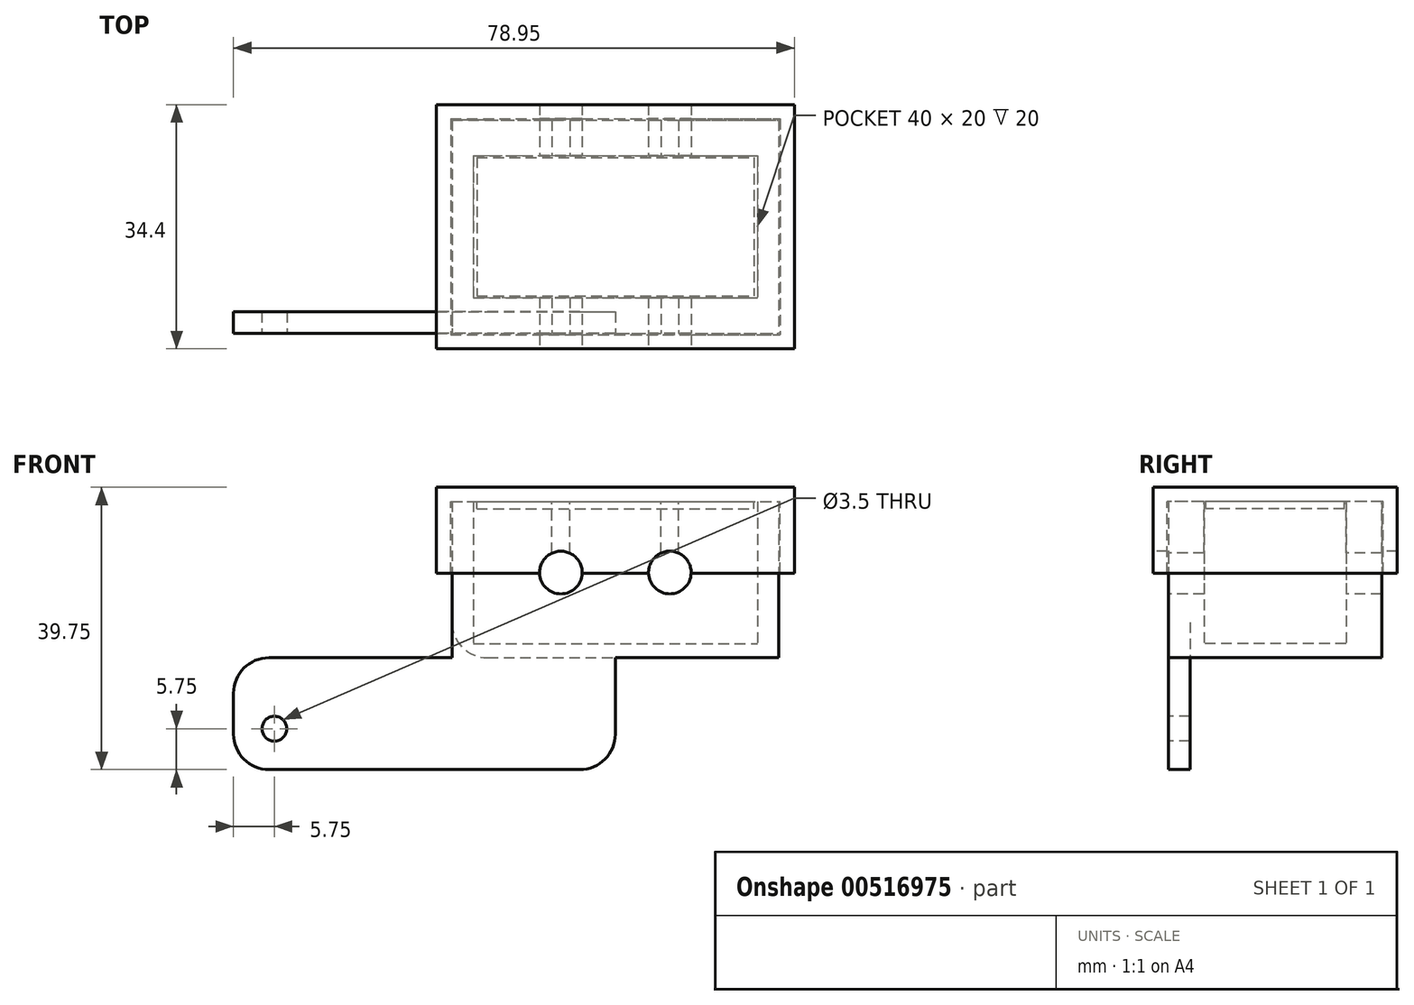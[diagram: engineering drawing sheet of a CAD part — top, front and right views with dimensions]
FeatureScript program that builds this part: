
annotation { "Feature Type Name" : "Feature", "Feature Type Description" : "" }
export const myFeature = defineFeature(function(context is Context, id is Id, definition is map)
    precondition{}
    {
        {
            var Q0;
            Q0=qCreatedBy(makeId("Top.planeOp"),FACE);
            var sketch = newSketch(context, id + "F0", { "sketchPlane" : qUnion([Q0])});
            skLineSegment(sketch, "E0.bottom", {"start": v(-20, 10) * mm, "end": v(20, 10) * mm});
            skLineSegment(sketch, "E0.top", {"start": v(-20, -10) * mm, "end": v(20, -10) * mm});
            skLineSegment(sketch, "E0.left", {"start": v(-20, 10) * mm, "end": v(-20, -10) * mm});
            skLineSegment(sketch, "E0.right", {"start": v(20, 10) * mm, "end": v(20, -10) * mm});
            skPoint(sketch, "E0.middle", {"position": v(0, 0) * mm});
            skLineSegment(sketch, "E1.bottom", {"start": v(-23, 15) * mm, "end": v(23, 15) * mm});
            skLineSegment(sketch, "E1.top", {"start": v(-23, -15) * mm, "end": v(23, -15) * mm});
            skLineSegment(sketch, "E1.left", {"start": v(-23, 15) * mm, "end": v(-23, -15) * mm});
            skLineSegment(sketch, "E1.right", {"start": v(23, 15) * mm, "end": v(23, -15) * mm});
            skSolve(sketch);
        }
        {
            var Q0;
            Q0=makeQuery(id+"F0.imprint","IMPRINT",FACE,{"disambiguationData":[TD([[makeQuery(id+"F0.imprint","IMPRINT",EDGE,{"derivedFrom":sQuery(id+"F0.wireOp",EDGE,"E0.bottom")}),1.0]])]});
            extrude(context, id + "F1", {"entities" : qUnion([Q0]), "depth" : 20 * mm, "offsetDistance" : 25 * mm});
        }
        {
            var Q0;
            Q0=makeQuery(id+"F1.opExtrude","SWEPT_FACE",FACE,{"disambiguationData":[OSD([sQuery(id+"F0.wireOp",EDGE,"E1.top")])]});
            var sketch = newSketch(context, id + "F2", { "sketchPlane" : qUnion([Q0])});
            skLineSegment(sketch, "E2", {"start": v(-23, 10) * mm, "end": v(-7.67, 10) * mm, "construction": true});
            skLineSegment(sketch, "E3", {"start": v(-7.67, 10) * mm, "end": v(7.67, 10) * mm, "construction": true});
            skLineSegment(sketch, "E4", {"start": v(7.67, 10) * mm, "end": v(23, 10) * mm, "construction": true});
            skCircle(sketch, "E5", {"center": v(-7.67, 10) * mm, "radius": 2.1 * mm});
            skCircle(sketch, "E6", {"center": v(7.67, 10) * mm, "radius": 2.1 * mm});
            skSolve(sketch);
        }
        {
            var Q0;
            Q0=makeQuery(id+"F2.imprint","IMPRINT",FACE,{"disambiguationData":[TD([[makeQuery(id+"F2.imprint","IMPRINT",EDGE,{"derivedFrom":sQuery(id+"F2.wireOp",EDGE,"E5")}),1.0]])]});
            var Q1;
            Q1=makeQuery(id+"F2.imprint","IMPRINT",FACE,{"disambiguationData":[TD([[makeQuery(id+"F2.imprint","IMPRINT",EDGE,{"derivedFrom":sQuery(id+"F2.wireOp",EDGE,"E6")}),1.0]])]});
            extrude(context, id + "F3", {"entities" : qUnion([Q0, Q1]), "operationType" : NewBodyOperationType.REMOVE, "endBound" : BoundingType.THROUGH_ALL, "oppositeDirection" : true, "depth" : 25 * mm, "offsetDistance" : 25 * mm});
        }
        {
            var Q0;
            Q0=makeQuery(id+"F1.opExtrude","SWEPT_FACE",FACE,{"disambiguationData":[OSD([sQuery(id+"F0.wireOp",EDGE,"E1.top")])]});
            var sketch = newSketch(context, id + "F4", { "sketchPlane" : qUnion([Q0])});
            skLineSegment(sketch, "E7.0.0", {"start": v(23, 0) * mm, "end": v(-23, 0) * mm, "construction": true});
            skLineSegment(sketch, "E7.0.1", {"start": v(-23, 0) * mm, "end": v(-23, 20) * mm, "construction": true});
            skLineSegment(sketch, "E7.0.2", {"start": v(-23, 20) * mm, "end": v(23, 20) * mm, "construction": true});
            skLineSegment(sketch, "E7.0.3", {"start": v(23, 20) * mm, "end": v(23, 0) * mm, "construction": true});
            skCircle(sketch, "E8.0", {"center": v(-7.67, 10) * mm, "radius": 2.1 * mm, "construction": true});
            skCircle(sketch, "E8.1", {"center": v(7.67, 10) * mm, "radius": 2.1 * mm, "construction": true});
            skLineSegment(sketch, "E9.bottom", {"start": v(-8.92, 10) * mm, "end": v(-6.42, 10) * mm});
            skLineSegment(sketch, "E9.top", {"start": v(-8.92, 23.75) * mm, "end": v(-6.42, 23.75) * mm});
            skLineSegment(sketch, "E9.left", {"start": v(-8.92, 23.75) * mm, "end": v(-8.92, 10) * mm});
            skLineSegment(sketch, "E9.right", {"start": v(-6.42, 23.75) * mm, "end": v(-6.42, 10) * mm});
            skLineSegment(sketch, "E10.bottom", {"start": v(6.42, 10) * mm, "end": v(8.92, 10) * mm});
            skLineSegment(sketch, "E10.top", {"start": v(6.42, 23.75) * mm, "end": v(8.92, 23.75) * mm});
            skLineSegment(sketch, "E10.left", {"start": v(6.42, 23.75) * mm, "end": v(6.42, 10) * mm});
            skLineSegment(sketch, "E10.right", {"start": v(8.92, 23.75) * mm, "end": v(8.92, 10) * mm});
            skSolve(sketch);
        }
        {
            var Q0;
            Q0 = qSketchRegion(id + "F4", true);
            extrude(context, id + "F5", {"entities" : qUnion([Q0]), "operationType" : NewBodyOperationType.REMOVE, "endBound" : BoundingType.THROUGH_ALL, "oppositeDirection" : true, "depth" : 25 * mm, "offsetDistance" : 25 * mm});
        }
        {
            var Q0;
            Q0=makeQuery(id+"F1.opExtrude","CAP_FACE",FACE,{"disambiguationData":[OSD([sQuery(id+"F0.wireOp",EDGE,"E0.bottom"),sQuery(id+"F0.wireOp",EDGE,"E0.top"),sQuery(id+"F0.wireOp",EDGE,"E0.left"),sQuery(id+"F0.wireOp",EDGE,"E0.right"),sQuery(id+"F0.wireOp",EDGE,"E1.bottom"),sQuery(id+"F0.wireOp",EDGE,"E1.top"),sQuery(id+"F0.wireOp",EDGE,"E1.left"),sQuery(id+"F0.wireOp",EDGE,"E1.right")])],"isStart":true});
            var sketch = newSketch(context, id + "F6", { "sketchPlane" : qUnion([Q0])});
            skLineSegment(sketch, "E11.0.0", {"start": v(-23, -15) * mm, "end": v(23, -15) * mm});
            skLineSegment(sketch, "E11.0.1", {"start": v(23, -15) * mm, "end": v(23, 15) * mm});
            skLineSegment(sketch, "E11.0.2", {"start": v(23, 15) * mm, "end": v(-23, 15) * mm});
            skLineSegment(sketch, "E11.0.3", {"start": v(-23, 15) * mm, "end": v(-23, -15) * mm});
            skSolve(sketch);
        }
        {
            var Q0;
            Q0 = qSketchRegion(id + "F6", true);
            extrude(context, id + "F7", {"entities" : qUnion([Q0]), "operationType" : NewBodyOperationType.ADD, "depth" : 2 * mm, "offsetDistance" : 25 * mm});
        }
        {
            var Q0;
            Q0=makeQuery(id+"F7.boolean.opBoolean","MERGE",FACE,{"derivedFrom":[makeQuery(id+"F1.opExtrude","SWEPT_FACE",FACE,{"disambiguationData":[OSD([sQuery(id+"F0.wireOp",EDGE,"E1.top")])]}),makeQuery(id+"F7.opExtrude","SWEPT_FACE",FACE,{"disambiguationData":[OSD([sQuery(id+"F6.wireOp",EDGE,"E11.0.2")])]})]});
            var sketch = newSketch(context, id + "F8", { "sketchPlane" : qUnion([Q0])});
            skLineSegment(sketch, "E12.bottom", {"start": v(0, -2) * mm, "end": v(-53.75, -2) * mm});
            skLineSegment(sketch, "E12.top", {"start": v(0, -17.75) * mm, "end": v(-53.75, -17.75) * mm});
            skLineSegment(sketch, "E12.left", {"start": v(0, -2) * mm, "end": v(0, -17.75) * mm});
            skLineSegment(sketch, "E12.right", {"start": v(-53.75, -2) * mm, "end": v(-53.75, -17.75) * mm});
            skLineSegment(sketch, "E13", {"start": v(-60.63, -12) * mm, "end": v(52.21, -12) * mm, "construction": true});
            skCircle(sketch, "E14", {"center": v(-48, -12) * mm, "radius": 1.75 * mm});
            skSolve(sketch);
        }
        {
            var Q0;
            Q0 = qSketchRegion(id + "F8", true);
            extrude(context, id + "F9", {"entities" : qUnion([Q0]), "operationType" : NewBodyOperationType.ADD, "oppositeDirection" : true, "depth" : 3 * mm, "offsetDistance" : 25 * mm});
        }
        {
            var Q0;
            Q0=makeQuery(id+"F9.opExtrude","SWEPT_EDGE",EDGE,{"disambiguationData":[OSD([sQuery(id+"F8.wireOp",EDGE,"E12.bottom"),sQuery(id+"F8.wireOp",EDGE,"E12.right")])]});
            var Q1;
            Q1=makeQuery(id+"F9.opExtrude","SWEPT_EDGE",EDGE,{"disambiguationData":[OSD([sQuery(id+"F8.wireOp",EDGE,"E12.top"),sQuery(id+"F8.wireOp",EDGE,"E12.right")])]});
            var Q2;
            {var subQ0=sQuery(id+"F6.wireOp",EDGE,"E11.0.3");Q2=makeQuery(id+"F9.boolean.opBoolean","SPLIT",EDGE,{"disambiguationData":[topologyDisambiguationEdgeConnected([makeQuery(id+"F9.opExtrude","SWEPT_FACE",FACE,{"disambiguationData":[OSD([sQuery(id+"F8.wireOp",EDGE,"E12.bottom")])]})])],"derivedFrom":makeQuery(id+"F7.opExtrude","CAP_EDGE",EDGE,{"disambiguationData":[OSD([subQ0])],"isStart":false})});}
            var Q3;
            Q3=makeQuery(id+"F9.opExtrude","SWEPT_EDGE",EDGE,{"disambiguationData":[OSD([sQuery(id+"F6.wireOp",EDGE,"E11.0.2"),sQuery(id+"F8.wireOp",EDGE,"E12.bottom"),sQuery(id+"F8.wireOp",EDGE,"E12.left")])]});
            var Q4;
            Q4=makeQuery(id+"F9.opExtrude","SWEPT_EDGE",EDGE,{"disambiguationData":[OSD([sQuery(id+"F8.wireOp",EDGE,"E12.top"),sQuery(id+"F8.wireOp",EDGE,"E12.left")])]});
            fillet(context, id + "F10", {"entities" : qUnion([Q0, Q1, Q2, Q3, Q4]), "tangentPropagation" : true, "radius" : 5 * mm, "defaultsChanged" : false, "vertexSettings" : [], "allowEdgeOverflow" : false});
        }
        {
            var Q0;
            {var subQ0=sQuery(id+"F0.wireOp",EDGE,"E1.bottom");var subQ1=sQuery(id+"F0.wireOp",EDGE,"E0.left");var subQ2=sQuery(id+"F0.wireOp",EDGE,"E0.top");var subQ3=sQuery(id+"F0.wireOp",EDGE,"E0.bottom");var subQ4=sQuery(id+"F0.wireOp",EDGE,"E1.top");var subQ5=sQuery(id+"F0.wireOp",EDGE,"E1.left");Q0=makeQuery(id+"F5.boolean.opBoolean","SPLIT",FACE,{"disambiguationData":[TD([makeQuery(id+"F1.opExtrude","SWEPT_FACE",FACE,{"disambiguationData":[OSD([subQ3])]}),makeQuery(id+"F1.opExtrude","SWEPT_FACE",FACE,{"disambiguationData":[OSD([subQ2])]}),makeQuery(id+"F1.opExtrude","SWEPT_FACE",FACE,{"disambiguationData":[OSD([subQ1])]}),makeQuery(id+"F1.opExtrude","SWEPT_FACE",FACE,{"disambiguationData":[OSD([subQ0])]}),makeQuery(id+"F1.opExtrude","SWEPT_FACE",FACE,{"disambiguationData":[OSD([subQ4])]}),makeQuery(id+"F1.opExtrude","SWEPT_FACE",FACE,{"disambiguationData":[OSD([subQ5])]}),makeQuery(id+"F5.opExtrude","SWEPT_FACE",FACE,{"disambiguationData":[OSD([sQuery(id+"F4.wireOp",EDGE,"E9.left")])]})])],"derivedFrom":makeQuery(id+"F1.opExtrude","CAP_FACE",FACE,{"disambiguationData":[OSD([subQ3,subQ2,subQ1,sQuery(id+"F0.wireOp",EDGE,"E0.right"),subQ0,subQ4,subQ5,sQuery(id+"F0.wireOp",EDGE,"E1.right")])],"isStart":false})});}
            var sketch = newSketch(context, id + "F11", { "sketchPlane" : qUnion([Q0])});
            skLineSegment(sketch, "E15.0", {"start": v(-23, 15) * mm, "end": v(-23, -15) * mm, "construction": true});
            skLineSegment(sketch, "E16.0", {"start": v(23, 15) * mm, "end": v(23, -15) * mm, "construction": true});
            skLineSegment(sketch, "E17.0", {"start": v(-6.42, 15) * mm, "end": v(6.42, 15) * mm, "construction": true});
            skLineSegment(sketch, "E18.0", {"start": v(-6.42, -15) * mm, "end": v(6.42, -15) * mm, "construction": true});
            skLineSegment(sketch, "E19.bottom", {"start": v(-23.2, 15.2) * mm, "end": v(23.2, 15.2) * mm});
            skLineSegment(sketch, "E19.top", {"start": v(-23.2, -15.2) * mm, "end": v(23.2, -15.2) * mm});
            skLineSegment(sketch, "E19.left", {"start": v(-23.2, 15.2) * mm, "end": v(-23.2, -15.2) * mm});
            skLineSegment(sketch, "E19.right", {"start": v(23.2, 15.2) * mm, "end": v(23.2, -15.2) * mm});
            skLineSegment(sketch, "E20.0.0", {"start": v(20, 10) * mm, "end": v(-20, 10) * mm, "construction": true});
            skLineSegment(sketch, "E20.0.1", {"start": v(-20, 10) * mm, "end": v(-20, -10) * mm, "construction": true});
            skLineSegment(sketch, "E20.0.2", {"start": v(-20, -10) * mm, "end": v(20, -10) * mm, "construction": true});
            skLineSegment(sketch, "E20.0.3", {"start": v(20, -10) * mm, "end": v(20, 10) * mm, "construction": true});
            skLineSegment(sketch, "E21.bottom", {"start": v(-25.2, 17.2) * mm, "end": v(25.2, 17.2) * mm});
            skLineSegment(sketch, "E21.top", {"start": v(-25.2, -17.2) * mm, "end": v(25.2, -17.2) * mm});
            skLineSegment(sketch, "E21.left", {"start": v(-25.2, 17.2) * mm, "end": v(-25.2, -17.2) * mm});
            skLineSegment(sketch, "E21.right", {"start": v(25.2, 17.2) * mm, "end": v(25.2, -17.2) * mm});
            skLineSegment(sketch, "E22.bottom", {"start": v(-19.5, 9.75) * mm, "end": v(19.5, 9.75) * mm});
            skLineSegment(sketch, "E22.top", {"start": v(-19.5, -9.75) * mm, "end": v(19.5, -9.75) * mm});
            skLineSegment(sketch, "E22.left", {"start": v(-19.5, 9.75) * mm, "end": v(-19.5, -9.75) * mm});
            skLineSegment(sketch, "E22.right", {"start": v(19.5, 9.75) * mm, "end": v(19.5, -9.75) * mm});
            skPoint(sketch, "E22.middle", {"position": v(0, 0) * mm});
            skSolve(sketch);
        }
        {
            var Q0;
            Q0=makeQuery(id+"F11.imprint","IMPRINT",FACE,{"disambiguationData":[TD([[makeQuery(id+"F11.imprint","IMPRINT",EDGE,{"derivedFrom":sQuery(id+"F11.wireOp",EDGE,"E19.bottom")}),1.0]])]});
            var Q1;
            Q1=makeQuery(id+"F11.imprint","IMPRINT",FACE,{"disambiguationData":[TD([[makeQuery(id+"F11.imprint","IMPRINT",EDGE,{"derivedFrom":sQuery(id+"F11.wireOp",EDGE,"E22.bottom")}),-1.0]])]});
            var Q2;
            {var subQ3=sQuery(id+"F0.wireOp",EDGE,"E0.left");Q2=makeQuery(id+"F11.imprint","IMPRINT",FACE,{"disambiguationData":[TD([[makeQuery(id+"F11.imprint","IMPRINT",EDGE,{"derivedFrom":makeQuery(id+"F1.opExtrude","CAP_EDGE",EDGE,{"disambiguationData":[OSD([subQ3])],"isStart":false})}),-1.0]])]});}
            var Q3;
            Q3=makeQuery(id+"F11.imprint","IMPRINT",FACE,{"disambiguationData":[TD([[makeQuery(id+"F11.imprint","IMPRINT",EDGE,{"derivedFrom":sQuery(id+"F11.wireOp",EDGE,"E19.bottom")}),-1.0]])]});
            extrude(context, id + "F12", {"entities" : qUnion([Q0, Q1, Q2, Q3]), "depth" : 2 * mm, "offsetDistance" : 25 * mm});
        }
        {
            var Q0;
            Q0=makeQuery(id+"F11.imprint","IMPRINT",FACE,{"disambiguationData":[TD([[makeQuery(id+"F11.imprint","IMPRINT",EDGE,{"derivedFrom":sQuery(id+"F11.wireOp",EDGE,"E22.bottom")}),-1.0]])]});
            extrude(context, id + "F13", {"entities" : qUnion([Q0]), "operationType" : NewBodyOperationType.ADD, "oppositeDirection" : true, "depth" : 1 * mm, "offsetDistance" : 25 * mm});
        }
        {
            var Q0;
            Q0=makeQuery(id+"F11.imprint","IMPRINT",FACE,{"disambiguationData":[TD([[makeQuery(id+"F11.imprint","IMPRINT",EDGE,{"derivedFrom":sQuery(id+"F11.wireOp",EDGE,"E19.bottom")}),1.0]])]});
            extrude(context, id + "F14", {"entities" : qUnion([Q0]), "operationType" : NewBodyOperationType.ADD, "oppositeDirection" : true, "depth" : 10.1 * mm, "offsetDistance" : 25 * mm});
        }
        {
            var Q0;
            {var subQ0=sQuery(id+"F11.wireOp",EDGE,"E21.top");Q0=makeQuery(id+"F14.boolean.opBoolean","MERGE",FACE,{"derivedFrom":[makeQuery(id+"F12.opExtrude","SWEPT_FACE",FACE,{"disambiguationData":[OSD([subQ0])]}),makeQuery(id+"F14.opExtrude","SWEPT_FACE",FACE,{"disambiguationData":[OSD([subQ0])]})]});}
            var sketch = newSketch(context, id + "F15", { "sketchPlane" : qUnion([Q0])});
            skArc(sketch, "E23.0", {"start": v(-8.92, 11.69) * mm, "mid": v(-7.67, 7.9) * mm, "end": v(-6.42, 11.69) * mm, "construction": true});
            skArc(sketch, "E24.0", {"start": v(6.42, 11.69) * mm, "mid": v(7.67, 7.9) * mm, "end": v(8.92, 11.69) * mm, "construction": true});
            skCircle(sketch, "E25", {"center": v(-7.67, 10) * mm, "radius": 3 * mm});
            skCircle(sketch, "E26", {"center": v(7.67, 10) * mm, "radius": 3 * mm});
            skSolve(sketch);
        }
        {
            var Q0;
            Q0 = qSketchRegion(id + "F15", true);
            extrude(context, id + "F16", {"entities" : qUnion([Q0]), "operationType" : NewBodyOperationType.REMOVE, "endBound" : BoundingType.THROUGH_ALL, "oppositeDirection" : true, "depth" : 25 * mm, "offsetDistance" : 25 * mm});
        }
    });
